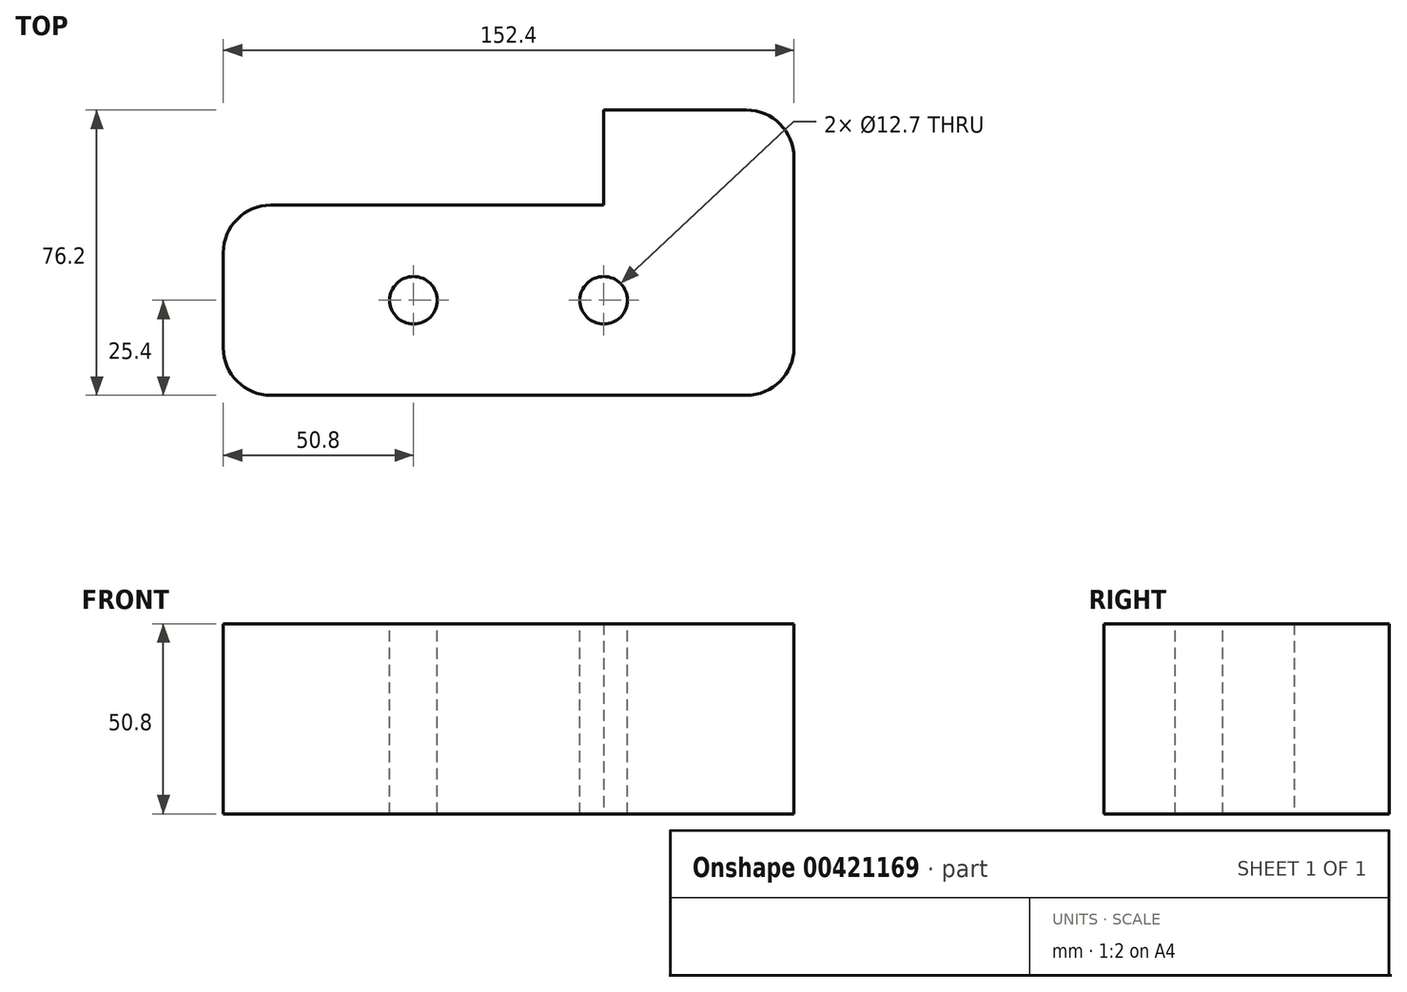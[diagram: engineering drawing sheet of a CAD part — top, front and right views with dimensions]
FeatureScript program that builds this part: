
annotation { "Feature Type Name" : "Feature", "Feature Type Description" : "" }
export const myFeature = defineFeature(function(context is Context, id is Id, definition is map)
    precondition{}
    {
        {
            var Q0;
            Q0=qCreatedBy(makeId("Top.planeOp"),FACE);
            var sketch = newSketch(context, id + "F0", { "sketchPlane" : qUnion([Q0])});
            skLineSegment(sketch, "E0", {"start": v(12.7, 0) * mm, "end": v(139.7, 0) * mm});
            skLineSegment(sketch, "E1", {"start": v(0, 12.7) * mm, "end": v(0, 38.1) * mm});
            skLineSegment(sketch, "E2", {"start": v(12.7, 50.8) * mm, "end": v(101.6, 50.8) * mm});
            skLineSegment(sketch, "E3", {"start": v(152.4, 12.7) * mm, "end": v(152.4, 63.5) * mm});
            skLineSegment(sketch, "E4", {"start": v(101.6, 50.8) * mm, "end": v(101.6, 76.2) * mm});
            skLineSegment(sketch, "E5", {"start": v(101.6, 76.2) * mm, "end": v(139.7, 76.2) * mm});
            skPoint(sketch, "E6.visualSharp", {"position": v(152.4, 76.2) * mm});
            skArc(sketch, "E6.filletArc", {"start": v(152.4, 63.5) * mm, "mid": v(148.68, 72.48) * mm, "end": v(139.7, 76.2) * mm});
            skPoint(sketch, "E7.visualSharp", {"position": v(152.4, 0) * mm});
            skArc(sketch, "E7.filletArc", {"start": v(139.7, 0) * mm, "mid": v(148.68, 3.72) * mm, "end": v(152.4, 12.7) * mm});
            skPoint(sketch, "E8.visualSharp", {"position": v(0, 0) * mm});
            skArc(sketch, "E8.filletArc", {"start": v(0, 12.7) * mm, "mid": v(3.72, 3.72) * mm, "end": v(12.7, 0) * mm});
            skPoint(sketch, "E9.visualSharp", {"position": v(0, 50.8) * mm});
            skArc(sketch, "E9.filletArc", {"start": v(12.7, 50.8) * mm, "mid": v(3.72, 47.08) * mm, "end": v(0, 38.1) * mm});
            skSolve(sketch);
        }
        {
            var Q0;
            Q0=makeQuery(id+"F0.imprint","IMPRINT",FACE,{"disambiguationData":[TD([[makeQuery(id+"F0.imprint","IMPRINT",EDGE,{"derivedFrom":sQuery(id+"F0.wireOp",EDGE,"E0")}),1.0]])]});
            extrude(context, id + "F1", {"entities" : qUnion([Q0]), "depth" : 50.8 * mm});
        }
        {
            var Q0;
            Q0=makeQuery(id+"F1.opExtrude","CAP_FACE",FACE,{"disambiguationData":[OSD([sQuery(id+"F0.wireOp",EDGE,"E0"),sQuery(id+"F0.wireOp",EDGE,"E1"),sQuery(id+"F0.wireOp",EDGE,"E2"),sQuery(id+"F0.wireOp",EDGE,"E3"),sQuery(id+"F0.wireOp",EDGE,"E4"),sQuery(id+"F0.wireOp",EDGE,"E5"),sQuery(id+"F0.wireOp",EDGE,"E6.filletArc"),sQuery(id+"F0.wireOp",EDGE,"E7.filletArc"),sQuery(id+"F0.wireOp",EDGE,"E8.filletArc"),sQuery(id+"F0.wireOp",EDGE,"E9.filletArc")])],"isStart":false});
            var sketch = newSketch(context, id + "F2", { "sketchPlane" : qUnion([Q0])});
            skPoint(sketch, "E10", {"position": v(50.8, 25.4) * mm});
            skPoint(sketch, "E10.positionSnap0", {"position": v(0, 25.4) * mm});
            skPoint(sketch, "E11", {"position": v(101.6, 25.4) * mm});
            skSolve(sketch);
        }
        {
            var Q0;
            Q0=sQuery(id+"F2.wireOp",VERTEX,"E10");
            var Q1;
            Q1=sQuery(id+"F2.wireOp",VERTEX,"E11");
            var Q2;
            Q2=makeQuery(id+"F1.opExtrude","SWEPT_BODY",BODY,{"disambiguationData":[OSD([sQuery(id+"F0.wireOp",EDGE,"E0"),sQuery(id+"F0.wireOp",EDGE,"E1"),sQuery(id+"F0.wireOp",EDGE,"E2"),sQuery(id+"F0.wireOp",EDGE,"E3"),sQuery(id+"F0.wireOp",EDGE,"E4"),sQuery(id+"F0.wireOp",EDGE,"E5"),sQuery(id+"F0.wireOp",EDGE,"E6.filletArc"),sQuery(id+"F0.wireOp",EDGE,"E7.filletArc"),sQuery(id+"F0.wireOp",EDGE,"E8.filletArc"),sQuery(id+"F0.wireOp",EDGE,"E9.filletArc")])]});
            hole(context, id + "F3", {"style" : HoleStyle.SIMPLE, "endStyle" : HoleEndStyle.THROUGH, "holeDiameter" : 12.7 * mm, "isTappedThrough" : true, "tappedDepth" : 12.7 * mm, "tapClearance" : 3, "locations" : qUnion([Q0, Q1]), "scope" : qUnion([Q2])});
        }
    });
